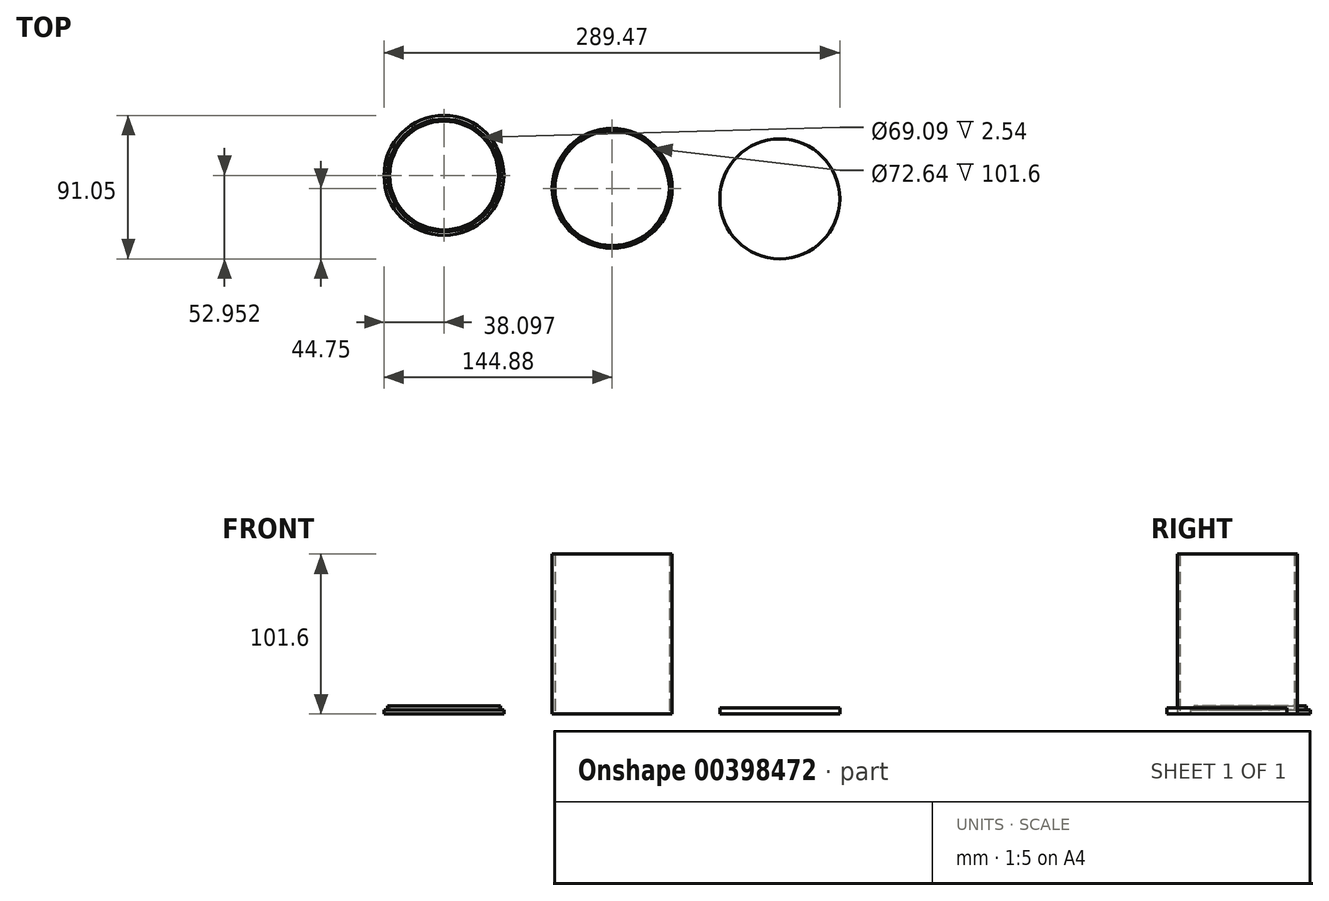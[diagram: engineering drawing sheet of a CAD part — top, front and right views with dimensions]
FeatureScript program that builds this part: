
annotation { "Feature Type Name" : "Feature", "Feature Type Description" : "" }
export const myFeature = defineFeature(function(context is Context, id is Id, definition is map)
    precondition{}
    {
        {
            var Q0;
            Q0=qCreatedBy(makeId("Top.planeOp"),FACE);
            var sketch = newSketch(context, id + "F0", { "sketchPlane" : qUnion([Q0])});
            skCircle(sketch, "E0", {"center": v(0, 0) * mm, "radius": 38.1 * mm});
            skCircle(sketch, "E1", {"center": v(0, 0) * mm, "radius": 36.32 * mm});
            skSolve(sketch);
        }
        {
            var Q0;
            Q0=makeQuery(id+"F0.imprint","IMPRINT",FACE,{"disambiguationData":[TD([[makeQuery(id+"F0.imprint","IMPRINT",EDGE,{"derivedFrom":sQuery(id+"F0.wireOp",EDGE,"E0")}),1.0]])]});
            extrude(context, id + "F1", {"entities" : qUnion([Q0]), "depth" : 101.6 * mm});
        }
        {
            var Q0;
            Q0=qCreatedBy(makeId("Top.planeOp"),FACE);
            var sketch = newSketch(context, id + "F2", { "sketchPlane" : qUnion([Q0])});
            skCircle(sketch, "E2", {"center": v(-106.78, 8.2) * mm, "radius": 38.1 * mm});
            skCircle(sketch, "E3", {"center": v(-106.78, 8.2) * mm, "radius": 35.81 * mm});
            skCircle(sketch, "E4", {"center": v(-106.78, 8.2) * mm, "radius": 34.54 * mm});
            skSolve(sketch);
        }
        {
            var Q0;
            Q0=makeQuery(id+"F2.imprint","IMPRINT",FACE,{"disambiguationData":[TD([[makeQuery(id+"F2.imprint","IMPRINT",EDGE,{"derivedFrom":sQuery(id+"F2.wireOp",EDGE,"E2")}),1.0]])]});
            extrude(context, id + "F3", {"entities" : qUnion([Q0]), "depth" : 2.54 * mm});
        }
        {
            var Q0;
            Q0=makeQuery(id+"F2.imprint","IMPRINT",FACE,{"disambiguationData":[TD([[makeQuery(id+"F2.imprint","IMPRINT",EDGE,{"derivedFrom":sQuery(id+"F2.wireOp",EDGE,"E3")}),1.0]])]});
            extrude(context, id + "F4", {"entities" : qUnion([Q0]), "operationType" : NewBodyOperationType.ADD, "depth" : 5.08 * mm});
        }
        {
            var Q0;
            Q0=makeQuery(id+"F2.imprint","IMPRINT",FACE,{"disambiguationData":[TD([[makeQuery(id+"F2.imprint","IMPRINT",EDGE,{"derivedFrom":sQuery(id+"F2.wireOp",EDGE,"E4")}),1.0]])]});
            extrude(context, id + "F5", {"entities" : qUnion([Q0]), "operationType" : NewBodyOperationType.ADD, "depth" : 2.54 * mm});
        }
        {
            var Q0;
            Q0=qCreatedBy(makeId("Top.planeOp"),FACE);
            var sketch = newSketch(context, id + "F6", { "sketchPlane" : qUnion([Q0])});
            skCircle(sketch, "E5", {"center": v(106.49, -6.65) * mm, "radius": 38.1 * mm});
            skSolve(sketch);
        }
        {
            var Q0;
            Q0=makeQuery(id+"F6.imprint","IMPRINT",FACE,{"disambiguationData":[TD([[makeQuery(id+"F6.imprint","IMPRINT",EDGE,{"derivedFrom":sQuery(id+"F6.wireOp",EDGE,"E5")}),1.0]])]});
            extrude(context, id + "F7", {"entities" : qUnion([Q0]), "depth" : 3.8 * mm});
        }
    });
